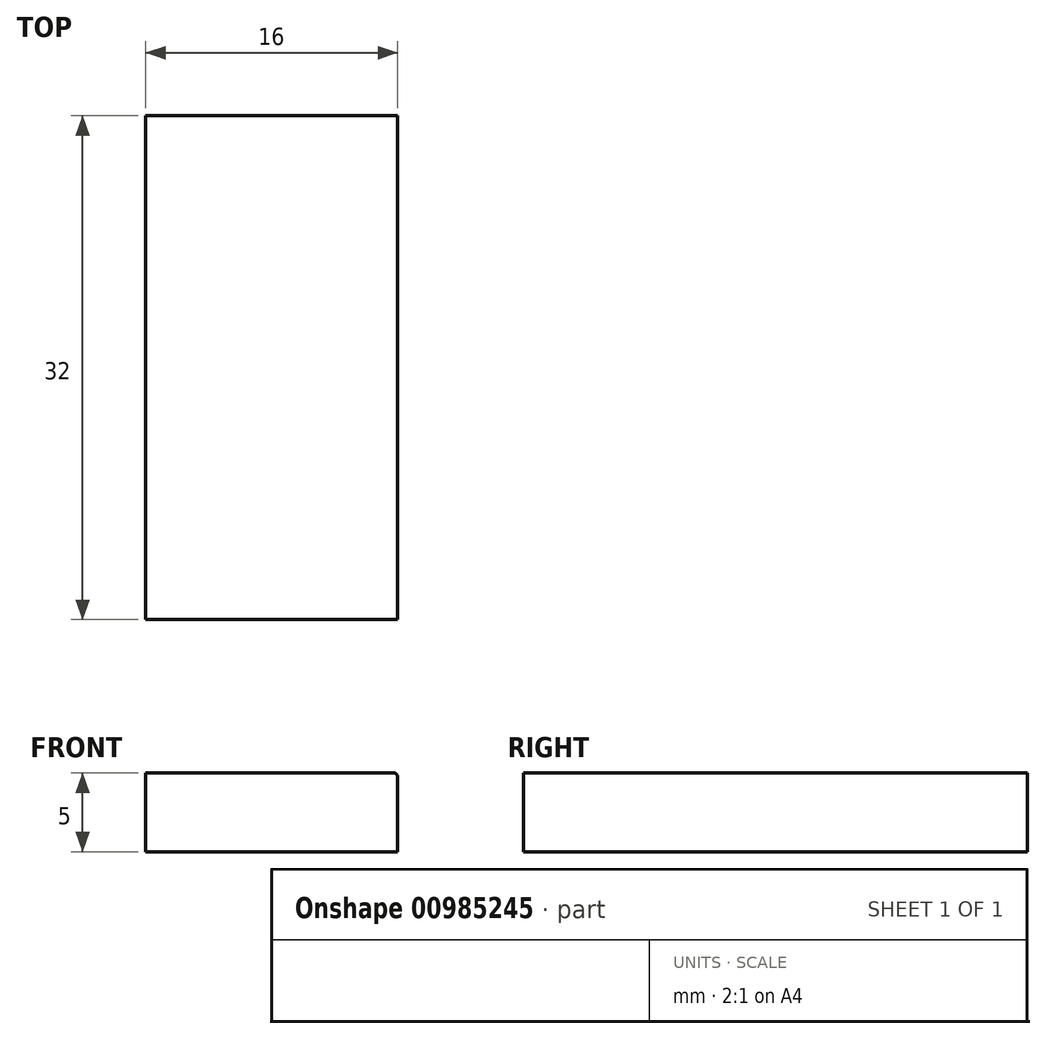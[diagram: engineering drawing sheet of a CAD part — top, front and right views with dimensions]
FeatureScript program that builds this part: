
annotation { "Feature Type Name" : "Feature", "Feature Type Description" : "" }
export const myFeature = defineFeature(function(context is Context, id is Id, definition is map)
    precondition{}
    {
        {
            var Q0;
            Q0=qCreatedBy(makeId("Top.planeOp"),FACE);
            var sketch = newSketch(context, id + "F0", { "sketchPlane" : qUnion([Q0])});
            skLineSegment(sketch, "E0.bottom", {"start": v(-10.66, 20.69) * mm, "end": v(-26.66, 20.69) * mm});
            skLineSegment(sketch, "E0.top", {"start": v(-10.66, -11.31) * mm, "end": v(-26.66, -11.31) * mm});
            skLineSegment(sketch, "E0.left", {"start": v(-10.66, 20.69) * mm, "end": v(-10.66, -11.31) * mm});
            skLineSegment(sketch, "E0.right", {"start": v(-26.66, 20.69) * mm, "end": v(-26.66, -11.31) * mm});
            skSolve(sketch);
        }
        {
            var Q0;
            Q0 = qSketchRegion(id + "F0", true);
            extrude(context, id + "F1", {"entities" : qUnion([Q0]), "depth" : 5 * mm, "offsetDistance" : 25.4 * mm});
        }
        {
            var Q0;
            Q0=makeQuery(id+"F1.opExtrude","CAP_FACE",FACE,{"disambiguationData":[OSD([sQuery(id+"F0.wireOp",EDGE,"E0.bottom"),sQuery(id+"F0.wireOp",EDGE,"E0.top"),sQuery(id+"F0.wireOp",EDGE,"E0.left"),sQuery(id+"F0.wireOp",EDGE,"E0.right")])],"isStart":false});
            var sketch = newSketch(context, id + "F2", { "sketchPlane" : qUnion([Q0])});
            skCircle(sketch, "E1", {"center": v(-22.76, 16.8) * mm, "radius": 2.35 * mm});
            skCircle(sketch, "E2.1.0.0", {"center": v(-14.76, 16.8) * mm, "radius": 2.35 * mm});
            skLineSegment(sketch, "E2.direction1", {"start": v(-22.76, 16.8) * mm, "end": v(-14.76, 16.8) * mm, "construction": true});
            skCircle(sketch, "E3.1.0.0", {"center": v(-22.76, 8.79) * mm, "radius": 2.35 * mm});
            skCircle(sketch, "E3.2.0.0", {"center": v(-22.77, 0.79) * mm, "radius": 2.35 * mm});
            skLineSegment(sketch, "E3.direction1", {"start": v(-22.76, 16.8) * mm, "end": v(-22.76, 8.79) * mm, "construction": true});
            skSolve(sketch);
        }
        {
            var Q0;
            Q0=sQuery(id+"F2.wireOp",EDGE,"E3.2.0.0");
            var Q1;
            Q1=sQuery(id+"F2.wireOp",EDGE,"E3.1.0.0");
            var Q2;
            Q2=sQuery(id+"F2.wireOp",EDGE,"E1");
            var Q3;
            Q3=sQuery(id+"F2.wireOp",EDGE,"E2.1.0.0");
            extrude(context, id + "F3", {"bodyType" : ToolBodyType.SURFACE, "surfaceEntities" : qUnion([Q0, Q1, Q2, Q3]), "depth" : 1.85 * mm, "offsetDistance" : 25.4 * mm});
        }
        {
            var Q0;
            Q0=makeQuery(id+"F1.opExtrude","CAP_EDGE",EDGE,{"disambiguationData":[OSD([sQuery(id+"F0.wireOp",EDGE,"E0.left")])],"isStart":false});
            var Q1;
            Q1=makeQuery(id+"F3.opExtrude","SWEPT_FACE",FACE,{"disambiguationData":[OSD([sQuery(id+"F2.wireOp",EDGE,"E3.2.0.0")])]});
            var Q2;
            Q2=makeQuery(id+"F3.opExtrude","SWEPT_FACE",FACE,{"disambiguationData":[OSD([sQuery(id+"F2.wireOp",EDGE,"E3.1.0.0")])]});
            var Q3;
            Q3=makeQuery(id+"F3.opExtrude","SWEPT_FACE",FACE,{"disambiguationData":[OSD([sQuery(id+"F2.wireOp",EDGE,"E1")])]});
            var Q4;
            Q4=makeQuery(id+"F3.opExtrude","SWEPT_FACE",FACE,{"disambiguationData":[OSD([sQuery(id+"F2.wireOp",EDGE,"E2.1.0.0")])]});
            fillet(context, id + "F4", {"entities" : qUnion([Q0, Q1, Q2, Q3, Q4]), "radius" : 0.25 * mm, "tangentPropagation" : true, "allowEdgeOverflow" : false});
        }
    });
